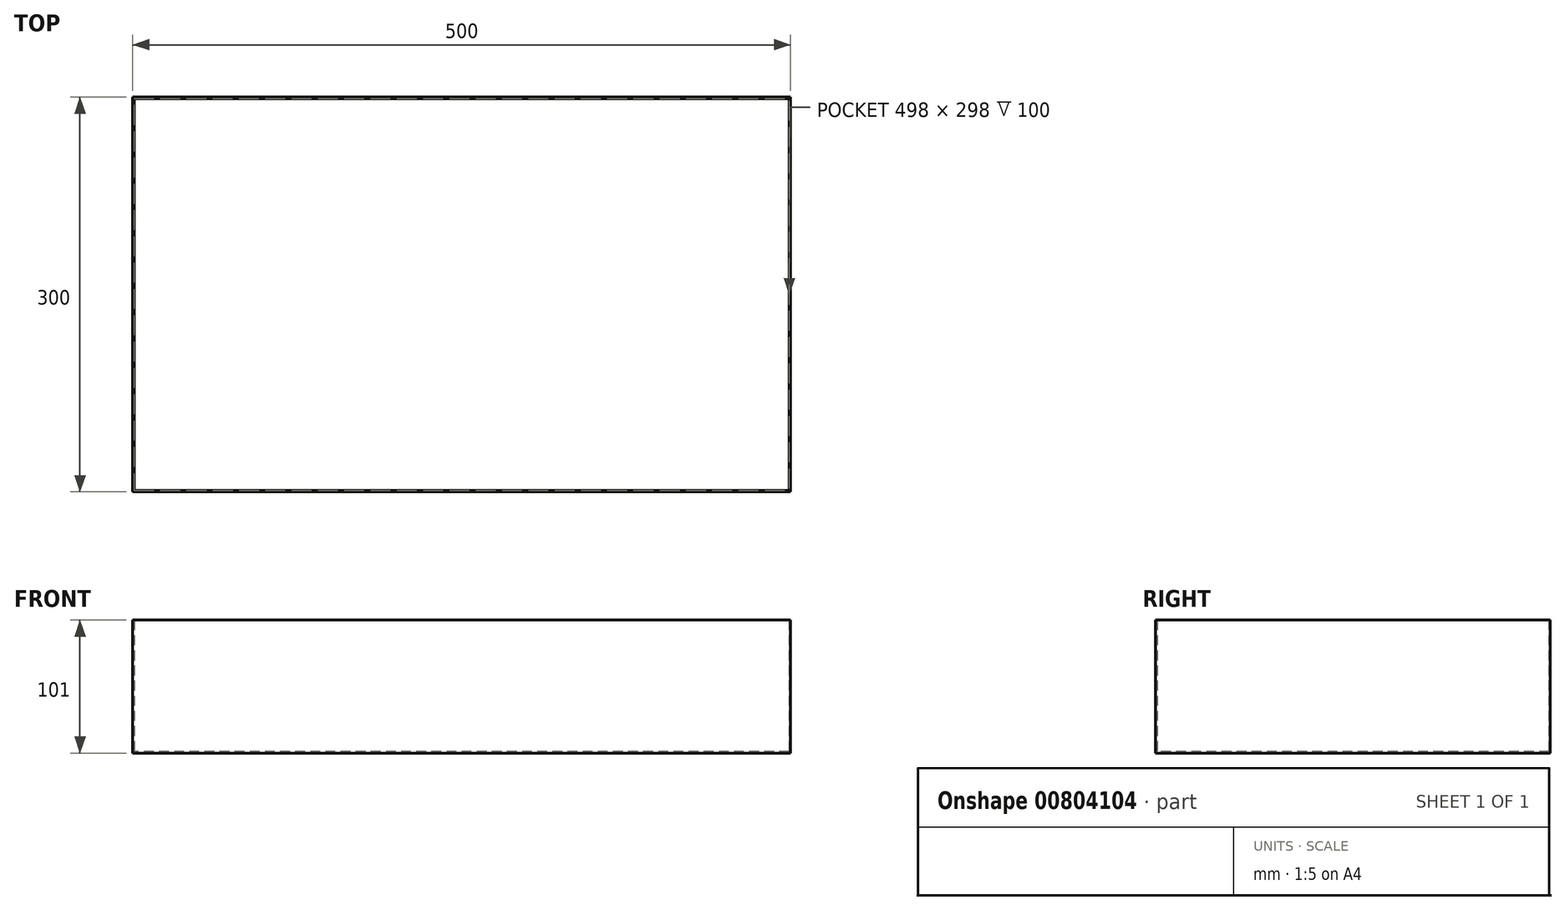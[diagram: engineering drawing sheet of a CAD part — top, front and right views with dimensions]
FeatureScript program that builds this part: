
annotation { "Feature Type Name" : "Feature", "Feature Type Description" : "" }
export const myFeature = defineFeature(function(context is Context, id is Id, definition is map)
    precondition{}
    {
        {
            var Q0;
            Q0=qCreatedBy(makeId("Top.planeOp"),FACE);
            var sketch = newSketch(context, id + "F0", { "sketchPlane" : qUnion([Q0])});
            skLineSegment(sketch, "E0.bottom", {"start": v(-250, 150) * mm, "end": v(250, 150) * mm});
            skLineSegment(sketch, "E0.top", {"start": v(-250, -150) * mm, "end": v(250, -150) * mm});
            skLineSegment(sketch, "E0.left", {"start": v(-250, 150) * mm, "end": v(-250, -150) * mm});
            skLineSegment(sketch, "E0.right", {"start": v(250, 150) * mm, "end": v(250, -150) * mm});
            skPoint(sketch, "E0.middle", {"position": v(0, 0) * mm});
            skSolve(sketch);
        }
        {
            var Q0;
            Q0=makeQuery(id+"F0.imprint","IMPRINT",FACE,{"disambiguationData":[TD([[makeQuery(id+"F0.imprint","IMPRINT",EDGE,{"derivedFrom":sQuery(id+"F0.wireOp",EDGE,"E0.bottom")}),-1.0]])]});
            extrude(context, id + "F1", {"entities" : qUnion([Q0]), "depth" : 1 * mm, "offsetDistance" : 25 * mm});
        }
        {
            var Q0;
            Q0=makeQuery(id+"F1.opExtrude","CAP_FACE",FACE,{"disambiguationData":[OSD([sQuery(id+"F0.wireOp",EDGE,"E0.bottom"),sQuery(id+"F0.wireOp",EDGE,"E0.top"),sQuery(id+"F0.wireOp",EDGE,"E0.left"),sQuery(id+"F0.wireOp",EDGE,"E0.right")])],"isStart":false});
            var sketch = newSketch(context, id + "F2", { "sketchPlane" : qUnion([Q0])});
            skLineSegment(sketch, "E1.bottom", {"start": v(-250, 150) * mm, "end": v(-249, 150) * mm});
            skLineSegment(sketch, "E1.top", {"start": v(-250, -150) * mm, "end": v(-249, -150) * mm});
            skLineSegment(sketch, "E1.left", {"start": v(-250, 150) * mm, "end": v(-250, -150) * mm});
            skLineSegment(sketch, "E1.right", {"start": v(-249, 150) * mm, "end": v(-249, -150) * mm});
            skLineSegment(sketch, "E2.bottom", {"start": v(250, -150) * mm, "end": v(-250, -150) * mm});
            skLineSegment(sketch, "E2.top", {"start": v(250, -149) * mm, "end": v(-250, -149) * mm});
            skLineSegment(sketch, "E2.left", {"start": v(250, -150) * mm, "end": v(250, -149) * mm});
            skLineSegment(sketch, "E2.right", {"start": v(-250, -150) * mm, "end": v(-250, -149) * mm});
            skLineSegment(sketch, "E3.bottom", {"start": v(250, -150) * mm, "end": v(249, -150) * mm});
            skLineSegment(sketch, "E3.top", {"start": v(250, 150) * mm, "end": v(249, 150) * mm});
            skLineSegment(sketch, "E3.left", {"start": v(250, -150) * mm, "end": v(250, 150) * mm});
            skLineSegment(sketch, "E3.right", {"start": v(249, -150) * mm, "end": v(249, 150) * mm});
            skLineSegment(sketch, "E4.bottom", {"start": v(250, 150) * mm, "end": v(-250, 150) * mm});
            skLineSegment(sketch, "E4.top", {"start": v(250, 149) * mm, "end": v(-250, 149) * mm});
            skLineSegment(sketch, "E4.left", {"start": v(250, 150) * mm, "end": v(250, 149) * mm});
            skLineSegment(sketch, "E4.right", {"start": v(-250, 150) * mm, "end": v(-250, 149) * mm});
            skSolve(sketch);
        }
        {
            var Q0;
            Q0 = qSketchRegion(id + "F2", true);
            extrude(context, id + "F3", {"entities" : qUnion([Q0]), "operationType" : NewBodyOperationType.ADD, "depth" : 100 * mm, "offsetDistance" : 25 * mm});
        }
    });
